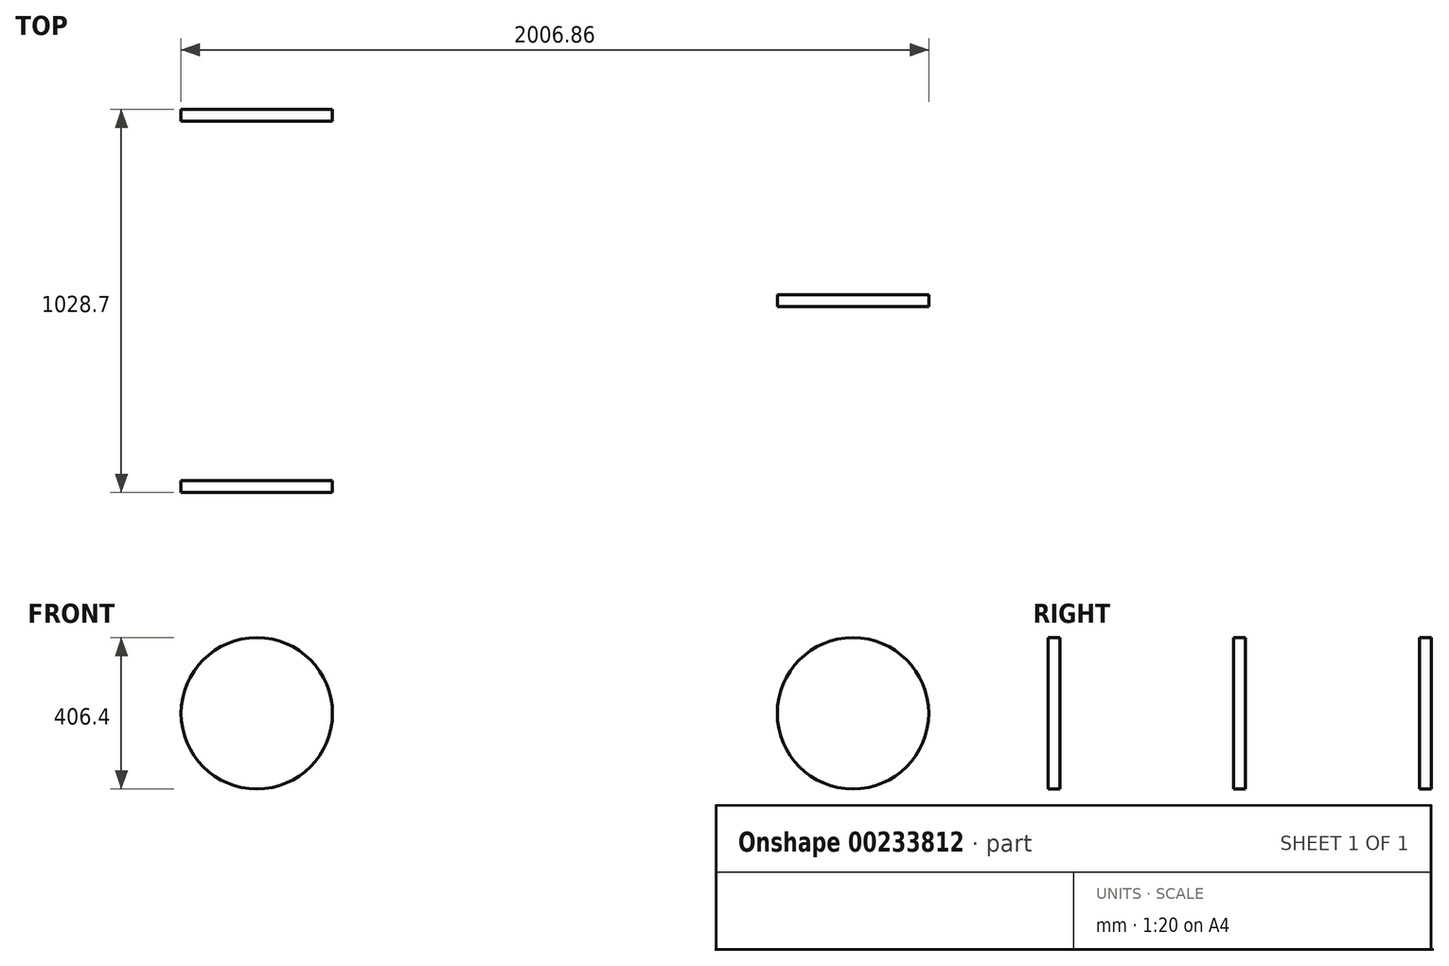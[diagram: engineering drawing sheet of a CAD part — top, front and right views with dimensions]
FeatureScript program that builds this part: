
annotation { "Feature Type Name" : "Feature", "Feature Type Description" : "" }
export const myFeature = defineFeature(function(context is Context, id is Id, definition is map)
    precondition{}
    {
        {
            var Q0;
            Q0=qCreatedBy(makeId("Front.planeOp"),FACE);
            var sketch = newSketch(context, id + "F0", { "sketchPlane" : qUnion([Q0])});
            skCircle(sketch, "E0", {"center": v(0, 0) * mm, "radius": 203.2 * mm});
            skSolve(sketch);
        }
        {
            var Q0;
            Q0=makeQuery(id+"F0.imprint","IMPRINT",FACE,{"disambiguationData":[TD([[makeQuery(id+"F0.imprint","IMPRINT",EDGE,{"derivedFrom":sQuery(id+"F0.wireOp",EDGE,"E0")}),1.0]])]});
            var Q1;
            Q1=sQuery(id+"F0.wireOp",EDGE,"E0");
            extrude(context, id + "F1", {"entities" : qUnion([Q0]), "surfaceEntities" : qUnion([Q1]), "endBound" : BoundingType.SYMMETRIC, "depth" : 31.75 * mm});
        }
        {
            var Q0;
            Q0=makeQuery(id+"F1.opExtrude","CAP_FACE",FACE,{"disambiguationData":[OSD([sQuery(id+"F0.wireOp",EDGE,"E0")])],"isStart":true});
            var sketch = newSketch(context, id + "F2", { "sketchPlane" : qUnion([Q0])});
            skLineSegment(sketch, "E1", {"start": v(0, 0) * mm, "end": v(91.02, 317.4) * mm});
            skLineSegment(sketch, "E2", {"start": v(91.02, 317.4) * mm, "end": v(1600.46, 0) * mm});
            skLineSegment(sketch, "E3", {"start": v(1371.86, 748.87) * mm, "end": v(1251.64, 177.17) * mm});
            skLineSegment(sketch, "E4", {"start": v(1251.64, 177.17) * mm, "end": v(903.65, 250.35) * mm});
            skCircle(sketch, "E5", {"center": v(345.02, 264) * mm, "radius": 124.98 * mm});
            skLineSegment(sketch, "E6.bottom", {"start": v(426.2, 359.02) * mm, "end": v(351, 359.02) * mm});
            skLineSegment(sketch, "E6.top", {"start": v(426.2, 388.84) * mm, "end": v(351, 388.84) * mm});
            skLineSegment(sketch, "E6.left", {"start": v(426.2, 359.02) * mm, "end": v(426.2, 388.84) * mm});
            skLineSegment(sketch, "E6.right", {"start": v(351, 359.02) * mm, "end": v(351, 388.84) * mm});
            skLineSegment(sketch, "E7.bottom", {"start": v(351, 139.16) * mm, "end": v(267.1, 139.16) * mm});
            skLineSegment(sketch, "E7.top", {"start": v(351, 166.28) * mm, "end": v(267.1, 166.28) * mm});
            skLineSegment(sketch, "E7.left", {"start": v(351, 139.16) * mm, "end": v(351, 166.28) * mm});
            skLineSegment(sketch, "E7.right", {"start": v(267.1, 139.16) * mm, "end": v(267.1, 166.28) * mm});
            skLineSegment(sketch, "E8", {"start": v(1371.86, 748.87) * mm, "end": v(1371.86, 952.07) * mm});
            skLineSegment(sketch, "E9", {"start": v(91.02, 317.4) * mm, "end": v(1031.15, 603.22) * mm});
            skSolve(sketch);
        }
        {
            var Q0;
            Q0=qCreatedBy(makeId("Right.planeOp"),FACE);
            var Q1;
            Q1=sQuery(id+"F2.wireOp",VERTEX,"E2.end");
            cPlane(context, id + "F3", {"entities" : qUnion([Q0, Q1]), "cplaneType" : CPlaneType.PLANE_POINT, "offset" : 25.4 * mm, "width" : 152.4 * mm, "height" : 152.4 * mm});
        }
        {
            var Q0;
            Q0=qCreatedBy(id+"F3.planeOp",FACE);
            var sketch = newSketch(context, id + "F4", { "sketchPlane" : qUnion([Q0])});
            skLineSegment(sketch, "E10", {"start": v(0, 0) * mm, "end": v(482.6, 0) * mm});
            skLineSegment(sketch, "E11", {"start": v(0, 0) * mm, "end": v(-482.6, 0) * mm});
            skSolve(sketch);
        }
        {
            var Q0;
            Q0=makeQuery(id+"F2.imprint","IMPRINT",FACE,{"disambiguationData":[TD([[makeQuery(id+"F2.imprint","IMPRINT",EDGE,{"derivedFrom":makeQuery(id+"F1.opExtrude","CAP_EDGE",EDGE,{"disambiguationData":[OSD([sQuery(id+"F0.wireOp",EDGE,"E0")])],"isStart":true})}),-1.0]])]});
            var Q1;
            Q1=sQuery(id+"F4.wireOp",VERTEX,"E10.end");
            cPlane(context, id + "F5", {"entities" : qUnion([Q0, Q1]), "cplaneType" : CPlaneType.PLANE_POINT, "offset" : 25.4 * mm, "width" : 152.4 * mm, "height" : 152.4 * mm});
        }
        {
            var Q0;
            Q0=makeQuery(id+"F2.imprint","IMPRINT",FACE,{"disambiguationData":[TD([[makeQuery(id+"F2.imprint","IMPRINT",EDGE,{"derivedFrom":makeQuery(id+"F1.opExtrude","CAP_EDGE",EDGE,{"disambiguationData":[OSD([sQuery(id+"F0.wireOp",EDGE,"E0")])],"isStart":true})}),-1.0]])]});
            var Q1;
            Q1=sQuery(id+"F4.wireOp",VERTEX,"E11.end");
            cPlane(context, id + "F6", {"entities" : qUnion([Q0, Q1]), "cplaneType" : CPlaneType.PLANE_POINT, "offset" : 25.4 * mm, "width" : 152.4 * mm, "height" : 152.4 * mm});
        }
        {
            var Q0;
            Q0=qCreatedBy(id+"F5.planeOp",FACE);
            var sketch = newSketch(context, id + "F7", { "sketchPlane" : qUnion([Q0])});
            skCircle(sketch, "E12", {"center": v(1600.46, 0) * mm, "radius": 203.2 * mm});
            skSolve(sketch);
        }
        {
            var Q0;
            Q0 = qSketchRegion(id + "F7", true);
            extrude(context, id + "F8", {"entities" : qUnion([Q0]), "depth" : 31.75 * mm});
        }
        {
            var Q0;
            Q0=qCreatedBy(id+"F6.planeOp",FACE);
            var sketch = newSketch(context, id + "F9", { "sketchPlane" : qUnion([Q0])});
            skCircle(sketch, "E13", {"center": v(1600.46, 0) * mm, "radius": 203.2 * mm});
            skSolve(sketch);
        }
        {
            var Q0;
            Q0 = qSketchRegion(id + "F9", true);
            extrude(context, id + "F10", {"entities" : qUnion([Q0]), "oppositeDirection" : true, "depth" : 31.75 * mm});
        }
        {
            var Q0;
            Q0=sQuery(id+"F2.wireOp",EDGE,"E4");
            var Q1;
            Q1=sQuery(id+"F2.wireOp",EDGE,"E3");
            var Q2;
            Q2=sQuery(id+"F2.wireOp",EDGE,"E8");
            extrude(context, id + "F11", {"bodyType" : ToolBodyType.SURFACE, "surfaceEntities" : qUnion([Q0, Q1, Q2]), "endBound" : BoundingType.SYMMETRIC, "depth" : 457.2 * mm});
        }
        {
            var Q0;
            Q0=sQuery(id+"F2.wireOp",EDGE,"E6.bottom");
            var Q1;
            Q1=sQuery(id+"F2.wireOp",EDGE,"E6.left");
            var Q2;
            Q2=sQuery(id+"F2.wireOp",EDGE,"E6.top");
            var Q3;
            Q3=sQuery(id+"F2.wireOp",EDGE,"E6.right");
            extrude(context, id + "F12", {"bodyType" : ToolBodyType.SURFACE, "surfaceEntities" : qUnion([Q0, Q1, Q2, Q3]), "depth" : 76.2 * mm});
        }
        {
            var Q0;
            Q0=sQuery(id+"F2.wireOp",EDGE,"E7.top");
            var Q1;
            Q1=sQuery(id+"F2.wireOp",EDGE,"E7.right");
            var Q2;
            Q2=sQuery(id+"F2.wireOp",EDGE,"E7.bottom");
            var Q3;
            Q3=sQuery(id+"F2.wireOp",EDGE,"E7.left");
            extrude(context, id + "F13", {"bodyType" : ToolBodyType.SURFACE, "surfaceEntities" : qUnion([Q0, Q1, Q2, Q3]), "oppositeDirection" : true, "depth" : 76.2 * mm});
        }
        {
            var Q0;
            Q0=sQuery(id+"F2.wireOp",VERTEX,"E9.end");
            var Q1;
            Q1=sQuery(id+"F2.wireOp",EDGE,"E9");
            cPlane(context, id + "F14", {"entities" : qUnion([Q0, Q1]), "cplaneType" : CPlaneType.LINE_POINT, "offset" : 25.4 * mm, "width" : 152.4 * mm, "height" : 152.4 * mm});
        }
    });
